# Revit family: Reece_Laundry Trough_Posh_Solus MK2_With Cabinet_45 L
name_source: partatom
category: Plumbing Fixtures
revit_build: Autodesk Revit 2018 (Build: 20181011_1500(x64)
units: mm (PartAtom-declared; Revit-internal decimal feet)

## family parameters
Always vertical = Yes
Cut with Voids When Loaded = No
Part Type = Normal
Room Calculation Point = Yes
Round Connector Dimension = Use Diameter
Shared = Yes
Work Plane-Based = Yes

## types (1)
- 1 Taphole_Single_Compact with Bypass and Overflow_Stainless Steel
    Default Elevation = 0 mm  [stored 0 ft]
    Description = Posh Solus MK2 45 Litre Compact Laundry Trough & Cabinet 1 Taphole with Bypass & Overflow Stainless Steel
    Disclaimer = THIS FILE IS THE PROPERTY OF THE REECE GROUP. IT MAY NOT BE REPRODUCED, REVERSE-ENGINEERED, OR MODIFIED. ANY REPUBLICATION, TRANSMISSION, OR DISTRIBUTION FOR THE PURPOSE OF COMMERCIALLY EXPLOITING THE FILES IS PROHIBITED.
    Keynote = Product #2406950, Reece_Laundry Trough_Posh_Solus MK2_With Cabinet_45 L - 1 Taphole_Single_Compact with Bypass and Overflow_Stainless Steel
    Manufacturer = Posh
    Model = Solus MK2
    Reece_Detail_Additional = Compact with Bypass and Overflow
    Reece_Detail_Disclaimer = THIS FILE IS THE PROPERTY OF THE REECE GROUP. IT MAY NOT BE REPRODUCED, REVERSE-ENGINEERED, OR MODIFIED. ANY REPUBLICATION, TRANSMISSION, OR DISTRIBUTION FOR THE PURPOSE OF COMMERCIALLY EXPLOITING THE FILES IS PROHIBITED.
    Reece_Material-Cabinet = Reece_Acrylic_White
    Reece_Material_Main = Reece_Metal_Steel
    Reece_Material_Secondary = Reece_Rubber_Black
    Reece_Overall_Capacity = 45 L
    Reece_Overall_Height = 912 mm
    Reece_Overall_Length = 600 mm
    Reece_Overall_Width = 500 mm
    Reece_Product_Brand = Posh
    Reece_Product_Description = Posh Solus MK2 45 Litre Compact Laundry Trough & Cabinet 1 Taphole with Bypass & Overflow Stainless Steel
    Reece_Product_Mount = Floor Mounted
    Reece_Product_Number = 2406950
    Reece_Product_Sub Brand = Solus MK2
    Reece_Product_Type = Laundry Trough
    Reece_Product_Web Page = https://www.reece.com.au
    Reece_Sink_Outlet = 40 mm  [stored 0.131234 ft]
    Type Comments = Laundry Trough
    URL = https://www.reece.com.au

note: [stored X ft] marks values corroborated as IEEE doubles in the binary element streams (Revit-internal decimal feet)

## geometry (parser evidence)
native form markers: Sweep x2
no freeform markers — native parametric forms only
